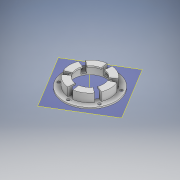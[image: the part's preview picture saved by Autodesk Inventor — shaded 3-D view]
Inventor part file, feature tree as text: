
AUTODESK INVENTOR PART (.ipt)
format: ipt  version: 2020 (Build 240168000, 168)  size: 258,560 bytes
history: native  units: mm
features: sketch x7, extrude x5, pattern_circular x4, revolve x2, other x1, plane x1
ambient origin geometry x8: Origin, YZ Plane, XZ Plane, XY Plane, X Axis, Y Axis, Z Axis, Center Point
bodies: Solid1 (feature_tree)
feature tree (20):
  extrude  "Extrusion1"  Depth=29.0mm
  sketch  "Sketch2"  dims[d2=6.0mm d3=0.0mm d4=3.5mm]
  other  "Work Axis1"
  revolve  "Revolution1"  [1 undecoded]
  pattern_circular  "Circular Pattern1"  Count=6 Angle=360.0deg
  plane  "Work Plane1"
  extrude  "Extrusion2"  Depth=1.0mm TaperAngle=0.0deg
  pattern_circular  "Circular Pattern2"  Count=6 Angle=360.0deg
  extrude  "Extrusion5"  Depth=1.0mm TaperAngle=0.0deg
  extrude  "Extrusion6"  Depth=1.0mm TaperAngle=0.0deg
  extrude  "Extrusion7"  Depth=1.0mm
  pattern_circular  "Circular Pattern3"  [2 undecoded]
  revolve  "Revolution2"  Angle=360.0deg
  pattern_circular  "Circular Pattern4"  [2 undecoded]
  sketch  "Sketch1"  dims[d0=23.0mm d1=29.0mm]
  sketch  "Sketch3"  dims[d5=1.0mm]
  sketch  "Sketch6"  dims[d6=90.0deg d7=60.0mm d8=360.0deg]
  sketch  "Sketch7"  dims[d10=31.5mm d11=1.0mm d12=0.0mm d16=60.0mm d17=360.0deg]
  sketch  "Sketch8"  dims[d22=2.0mm d23=1.0mm d24=0.0mm]
  sketch  "Sketch9"  dims[d25=37.0mm d26=1.0mm d27=0.0mm d28=2.0mm d29=1.0mm d30=0.0mm d31=60.0mm d32=360.0deg d34=5.0mm d35=1.0mm d36=90.0deg d37=60.0mm d38=360.0deg d13=0.5mm d14=0.872665mm]
note: 5 required parameter values undecoded (feature->parameter linkage not recoverable at this tier; creation-order binding heuristic only, values carry confidence <= 0.55)